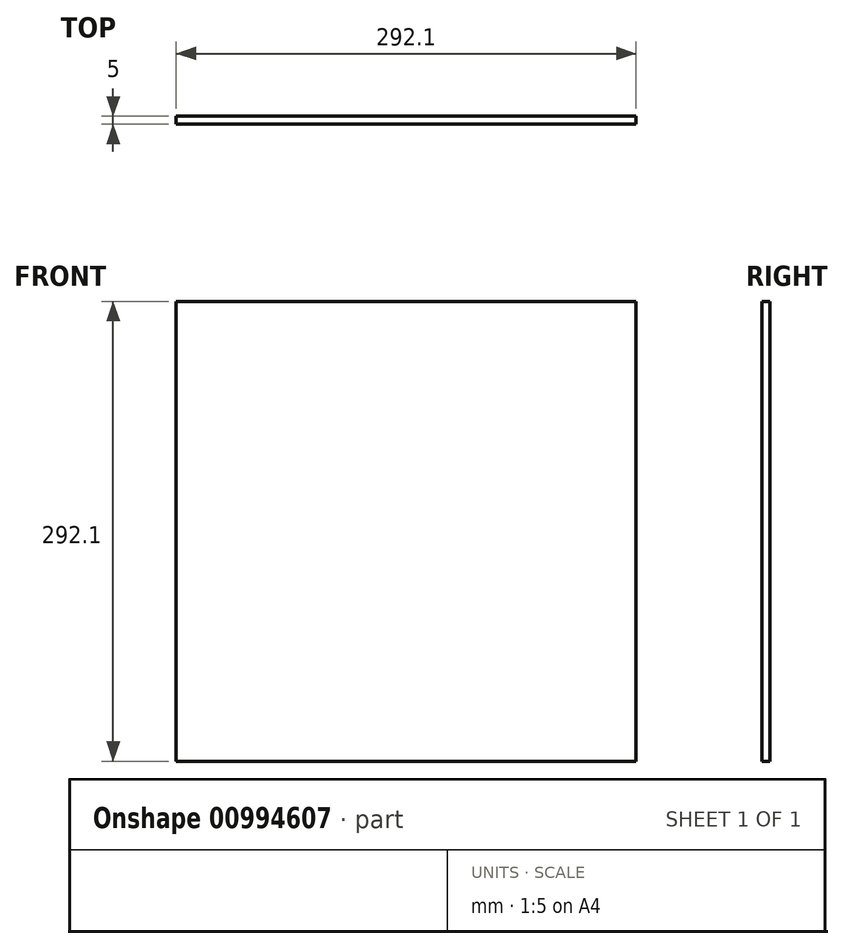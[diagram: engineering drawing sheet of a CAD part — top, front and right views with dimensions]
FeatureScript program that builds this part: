
annotation { "Feature Type Name" : "Feature", "Feature Type Description" : "" }
export const myFeature = defineFeature(function(context is Context, id is Id, definition is map)
    precondition{}
    {
        {
            var Q0;
            Q0=qCreatedBy(makeId("Front.planeOp"),FACE);
            var sketch = newSketch(context, id + "F0", { "sketchPlane" : qUnion([Q0])});
            skLineSegment(sketch, "E0.bottom", {"start": v(-146.05, -146.05) * mm, "end": v(146.05, -146.05) * mm});
            skLineSegment(sketch, "E0.top", {"start": v(-146.05, 146.05) * mm, "end": v(146.05, 146.05) * mm});
            skLineSegment(sketch, "E0.left", {"start": v(-146.05, -146.05) * mm, "end": v(-146.05, 146.05) * mm});
            skLineSegment(sketch, "E0.right", {"start": v(146.05, -146.05) * mm, "end": v(146.05, 146.05) * mm});
            skPoint(sketch, "E0.middle", {"position": v(0, 0) * mm});
            skSolve(sketch);
        }
        {
            var Q0;
            Q0=makeQuery(id+"F0.imprint","IMPRINT",FACE,{"disambiguationData":[TD([[makeQuery(id+"F0.imprint","IMPRINT",EDGE,{"derivedFrom":sQuery(id+"F0.wireOp",EDGE,"E0.bottom")}),1.0]])]});
            extrude(context, id + "F1", {"entities" : qUnion([Q0]), "depth" : 5 * mm, "offsetDistance" : 25 * mm});
        }
    });
